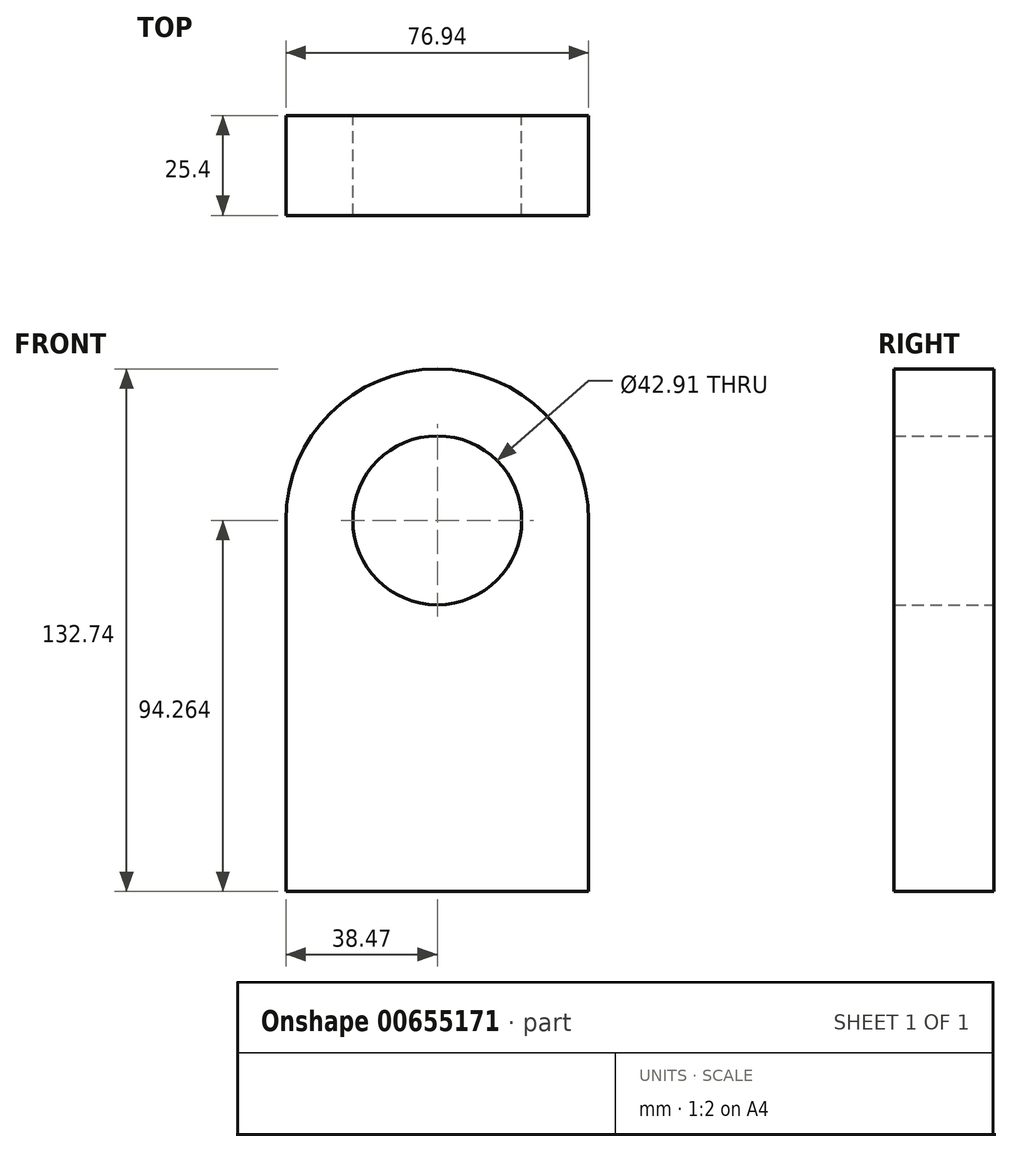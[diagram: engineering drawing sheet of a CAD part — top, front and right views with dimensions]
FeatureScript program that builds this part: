
annotation { "Feature Type Name" : "Feature", "Feature Type Description" : "" }
export const myFeature = defineFeature(function(context is Context, id is Id, definition is map)
    precondition{}
    {
        {
            var Q0;
            Q0=qCreatedBy(makeId("Front.planeOp"),FACE);
            var sketch = newSketch(context, id + "F0", { "sketchPlane" : qUnion([Q0])});
            skLineSegment(sketch, "E0.top", {"start": v(38.47, -47.13) * mm, "end": v(-38.47, -47.13) * mm});
            skLineSegment(sketch, "E0.left", {"start": v(38.47, 47.13) * mm, "end": v(38.47, -47.13) * mm});
            skLineSegment(sketch, "E0.right", {"start": v(-38.47, 47.13) * mm, "end": v(-38.47, -47.13) * mm});
            skPoint(sketch, "E0.middle", {"position": v(0, 0) * mm});
            skArc(sketch, "E1", {"start": v(38.47, 47.13) * mm, "mid": v(0, 85.6) * mm, "end": v(-38.47, 47.13) * mm});
            skCircle(sketch, "E2", {"center": v(0, 47.13) * mm, "radius": 21.45 * mm});
            skSolve(sketch);
        }
        {
            var Q0;
            Q0 = qSketchRegion(id + "F0", true);
            extrude(context, id + "F1", {"entities" : qUnion([Q0]), "depth" : 25.4 * mm, "offsetDistance" : 25.4 * mm});
        }
    });
